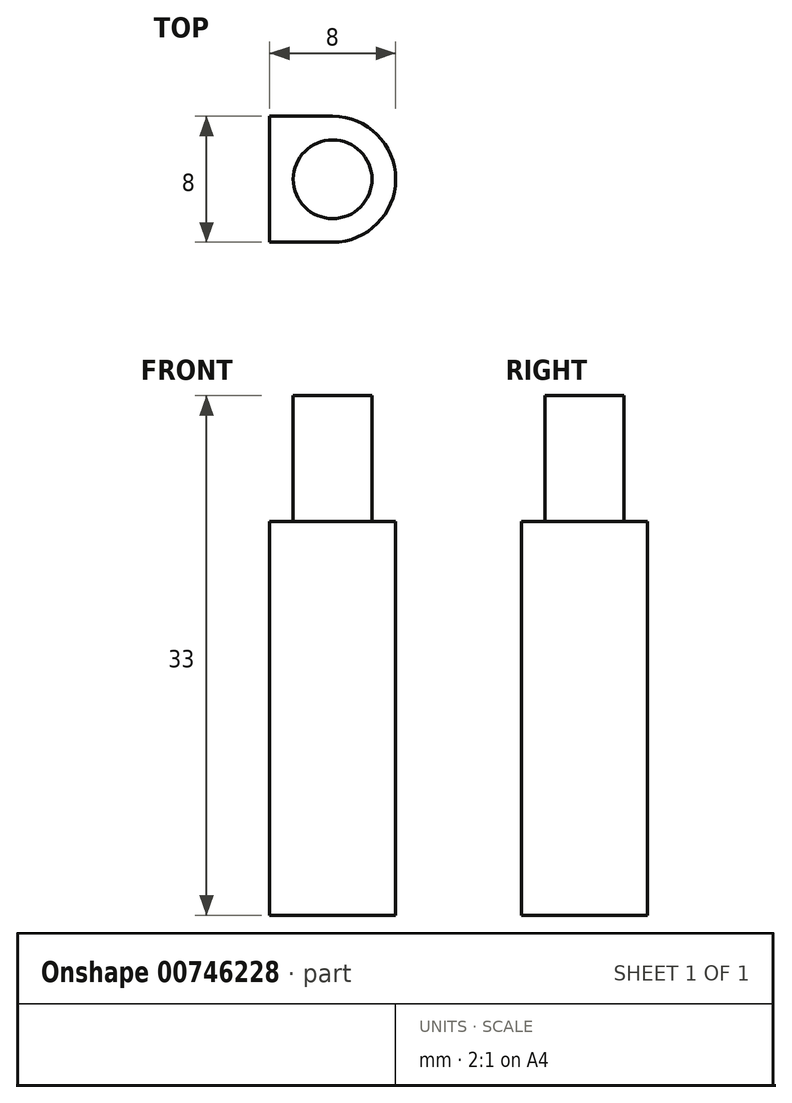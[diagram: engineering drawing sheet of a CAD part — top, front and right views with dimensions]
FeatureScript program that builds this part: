
annotation { "Feature Type Name" : "Feature", "Feature Type Description" : "" }
export const myFeature = defineFeature(function(context is Context, id is Id, definition is map)
    precondition{}
    {
        {
            var Q0;
            Q0=qCreatedBy(makeId("Top.planeOp"),FACE);
            var sketch = newSketch(context, id + "F0", { "sketchPlane" : qUnion([Q0])});
            skCircle(sketch, "E0", {"center": v(0, 0) * mm, "radius": 4 * mm});
            skCircle(sketch, "E1", {"center": v(0, 0) * mm, "radius": 2.5 * mm});
            skLineSegment(sketch, "E2.bottom", {"start": v(0, 4) * mm, "end": v(-4, 4) * mm});
            skLineSegment(sketch, "E2.top", {"start": v(0, -4) * mm, "end": v(-4, -4) * mm});
            skLineSegment(sketch, "E2.left", {"start": v(0, 4) * mm, "end": v(0, -4) * mm});
            skLineSegment(sketch, "E2.right", {"start": v(-4, 4) * mm, "end": v(-4, -4) * mm});
            skSolve(sketch);
        }
        {
            var Q0;
            {var subQ0=sQuery(id+"F0.wireOp",EDGE,"E2.left");var subQ3=sQuery(id+"F0.wireOp",EDGE,"E1");var subQ4=makeQuery(id+"F0.imprint","INTERSECT",VERTEX,{"disambiguationData":[OD(0.0)],"derivedFrom":[subQ3,subQ0]});Q0=makeQuery(id+"F0.imprint","IMPRINT",FACE,{"disambiguationData":[TD([[makeQuery(id+"F0.imprint","IMPRINT",EDGE,{"disambiguationData":[TD([[subQ4,-1.0]])],"derivedFrom":subQ3}),-1.0]])]});}
            var Q1;
            {var subQ0=sQuery(id+"F0.wireOp",EDGE,"E2.left");var subQ4=sQuery(id+"F0.wireOp",EDGE,"E1");var subQ5=makeQuery(id+"F0.imprint","INTERSECT",VERTEX,{"disambiguationData":[OD(0.0)],"derivedFrom":[subQ4,subQ0]});Q1=makeQuery(id+"F0.imprint","IMPRINT",FACE,{"disambiguationData":[TD([[makeQuery(id+"F0.imprint","IMPRINT",EDGE,{"disambiguationData":[TD([[subQ5,1.0]])],"derivedFrom":subQ4}),-1.0]])]});}
            var Q2;
            {var subQ0=sQuery(id+"F0.wireOp",EDGE,"E2.top");Q2=makeQuery(id+"F0.imprint","IMPRINT",FACE,{"disambiguationData":[TD([[makeQuery(id+"F0.imprint","IMPRINT",EDGE,{"derivedFrom":subQ0}),-1.0]])]});}
            var Q3;
            {var subQ0=sQuery(id+"F0.wireOp",EDGE,"E2.bottom");Q3=makeQuery(id+"F0.imprint","IMPRINT",FACE,{"disambiguationData":[TD([[makeQuery(id+"F0.imprint","IMPRINT",EDGE,{"derivedFrom":subQ0}),1.0]])]});}
            var Q4;
            {var subQ0=sQuery(id+"F0.wireOp",EDGE,"E2.left");var subQ1=sQuery(id+"F0.wireOp",EDGE,"E1");var subQ2=makeQuery(id+"F0.imprint","INTERSECT",VERTEX,{"disambiguationData":[OD(0.0)],"derivedFrom":[subQ1,subQ0]});Q4=makeQuery(id+"F0.imprint","IMPRINT",FACE,{"disambiguationData":[TD([[makeQuery(id+"F0.imprint","IMPRINT",EDGE,{"disambiguationData":[TD([[subQ2,-1.0]])],"derivedFrom":subQ1}),1.0]])]});}
            var Q5;
            {var subQ0=sQuery(id+"F0.wireOp",EDGE,"E2.left");var subQ1=sQuery(id+"F0.wireOp",EDGE,"E1");var subQ2=makeQuery(id+"F0.imprint","INTERSECT",VERTEX,{"disambiguationData":[OD(0.0)],"derivedFrom":[subQ1,subQ0]});Q5=makeQuery(id+"F0.imprint","IMPRINT",FACE,{"disambiguationData":[TD([[makeQuery(id+"F0.imprint","IMPRINT",EDGE,{"disambiguationData":[TD([[subQ2,1.0]])],"derivedFrom":subQ1}),1.0]])]});}
            extrude(context, id + "F1", {"entities" : qUnion([Q0, Q1, Q2, Q3, Q4, Q5]), "depth" : -25 * mm, "offsetDistance" : 25 * mm});
        }
        {
            var Q0;
            {var subQ0=sQuery(id+"F0.wireOp",EDGE,"E2.left");var subQ1=sQuery(id+"F0.wireOp",EDGE,"E1");var subQ2=makeQuery(id+"F0.imprint","INTERSECT",VERTEX,{"disambiguationData":[OD(0.0)],"derivedFrom":[subQ1,subQ0]});Q0=makeQuery(id+"F0.imprint","IMPRINT",FACE,{"disambiguationData":[TD([[makeQuery(id+"F0.imprint","IMPRINT",EDGE,{"disambiguationData":[TD([[subQ2,1.0]])],"derivedFrom":subQ1}),1.0]])]});}
            var Q1;
            {var subQ0=sQuery(id+"F0.wireOp",EDGE,"E2.left");var subQ1=sQuery(id+"F0.wireOp",EDGE,"E1");var subQ2=makeQuery(id+"F0.imprint","INTERSECT",VERTEX,{"disambiguationData":[OD(0.0)],"derivedFrom":[subQ1,subQ0]});Q1=makeQuery(id+"F0.imprint","IMPRINT",FACE,{"disambiguationData":[TD([[makeQuery(id+"F0.imprint","IMPRINT",EDGE,{"disambiguationData":[TD([[subQ2,-1.0]])],"derivedFrom":subQ1}),1.0]])]});}
            extrude(context, id + "F2", {"entities" : qUnion([Q0, Q1]), "operationType" : NewBodyOperationType.ADD, "depth" : 8 * mm, "offsetDistance" : 25 * mm});
        }
    });
